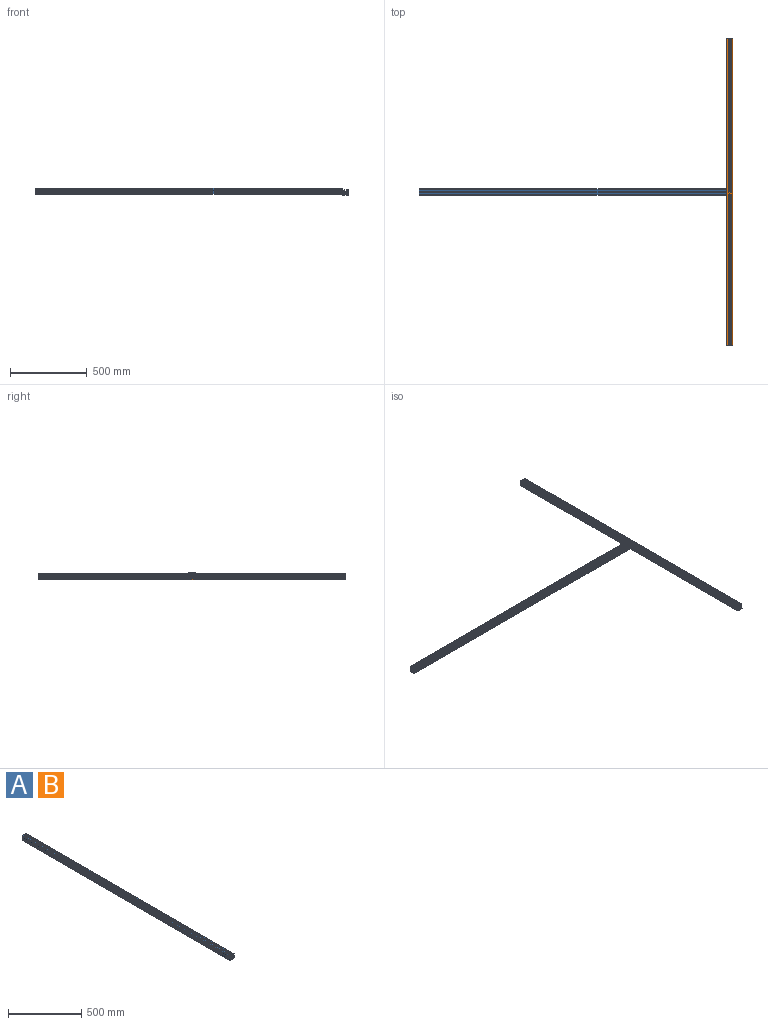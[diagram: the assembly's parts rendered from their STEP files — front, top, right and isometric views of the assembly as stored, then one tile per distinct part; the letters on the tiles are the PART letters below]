
ASSEMBLY  parts=2 mates=1
PART A: 155 faces, bbox 40x2000x40 mm
  f0: cylinder r=3.4mm len=2000mm, axis (0,-1,0), area 42725.7mm2, adj f1,f2
  f1: plane 40x40mm, normal (0,-1,0), area 657mm2, adj f0,f3,f4,f5,f6,f7,f8,f9
  f2: plane 40x40mm, normal (0,1,0), area 657mm2, adj f0,f3,f4,f5,f6,f7,f8,f9
  f3: cylinder r=1.5mm len=2000mm, axis (0,-1,0), area 4712.4mm2, adj f1,f2,f4,f122
  f4: plane 2000x10.5mm, normal (-1,0,0), area 21000mm2, adj f1,f2,f3,f5
  f5: cylinder r=4mm len=2000mm, axis (0,-1,0), area 12566.4mm2, adj f1,f2,f4,f6
  f6: plane 2000x10.5mm, normal (0,0,-1), area 21000mm2, adj f1,f2,f5,f7
  f7: cylinder r=1.5mm len=2000mm, axis (0,-1,0), area 4712.4mm2, adj f1,f2,f6,f8
  f8: plane 2000x2mm, normal (1,0,0), area 4000mm2, adj f1,f2,f7,f9
  f9: cylinder r=1mm len=2000mm, axis (0,-1,0), area 3141.6mm2, adj f1,f2,f8,f10
  f10: plane 2000x1.5mm, normal (0,0,1), area 3000mm2, adj f1,f2,f9,f11
  f11: cylinder r=0.5mm len=2000mm, axis (0,-1,0), area 1570.8mm2, adj f1,f2,f10,f12
  f12: plane 2000x1.55mm, normal (-1,0,0), area 3100mm2, adj f1,f2,f11,f13
  f13: cylinder r=0.45mm len=2000mm, axis (0,-1,0), area 1413.7mm2, adj f1,f2,f12,f14
  f14: plane 2000x0.05mm, normal (0,0,1), area 100mm2, adj f1,f2,f13,f15
  f15: cylinder r=2.5mm len=2000mm, axis (0,-1,0), area 7854mm2, adj f1,f2,f14,f16
  f16: plane 2000x1.31mm, normal (1,0,0), area 2615.2mm2, adj f1,f2,f15,f17
  f17: cylinder r=5mm len=2000mm, axis (0,-1,0), area 7854mm2, adj f1,f2,f16,f18
  f18: plane 2000x1.44mm, normal (0.71,0,-0.71), area 4079.7mm2, adj f1,f2,f17,f19
  f19: cylinder r=5mm len=2000mm, axis (0,-1,0), area 7854mm2, adj f1,f2,f18,f20
  f20: plane 2000x7.12mm, normal (0,0,-1), area 14230.4mm2, adj f1,f2,f19,f21
  f21: cylinder r=5mm len=2000mm, axis (0,-1,0), area 7854mm2, adj f1,f2,f20,f22
  f22: plane 2000x1.44mm, normal (-0.71,0,-0.71), area 4079.7mm2, adj f1,f2,f21,f23
  f23: cylinder r=5mm len=2000mm, axis (0,-1,0), area 7854mm2, adj f1,f2,f22,f24
  f24: plane 2000x1.31mm, normal (-1,0,0), area 2615.2mm2, adj f1,f2,f23,f25
  f25: cylinder r=2.5mm len=2000mm, axis (0,-1,0), area 7854mm2, adj f1,f2,f24,f26
  f26: plane 2000x0.05mm, normal (0,0,1), area 100mm2, adj f1,f2,f25,f27
  f27: cylinder r=0.45mm len=2000mm, axis (0,-1,0), area 1413.7mm2, adj f1,f2,f26,f28
  f28: plane 2000x1.55mm, normal (1,0,0), area 3100mm2, adj f1,f2,f27,f29
  f29: cylinder r=0.5mm len=2000mm, axis (0,-1,0), area 1570.8mm2, adj f1,f2,f28,f30
  f30: plane 2000x1.5mm, normal (0,0,1), area 3000mm2, adj f1,f2,f29,f31
  f31: cylinder r=1mm len=2000mm, axis (0,-1,0), area 3141.6mm2, adj f1,f2,f30,f32
  f32: plane 2000x2mm, normal (-1,0,0), area 4000mm2, adj f1,f2,f31,f33
  f33: cylinder r=1.5mm len=2000mm, axis (0,-1,0), area 4712.4mm2, adj f1,f2,f32,f34
  f34: plane 2000x10.5mm, normal (0,0,-1), area 21000mm2, adj f1,f2,f33,f35
  f35: cylinder r=4mm len=2000mm, axis (0,-1,0), area 12566.4mm2, adj f1,f2,f34,f36
  f36: plane 2000x10.5mm, normal (1,0,0), area 21000mm2, adj f1,f2,f35,f37
  f37: cylinder r=1.5mm len=2000mm, axis (0,-1,0), area 4712.4mm2, adj f1,f2,f36,f38
  f38: plane 2000x2mm, normal (0,0,1), area 4000mm2, adj f1,f2,f37,f39
  f39: cylinder r=1mm len=2000mm, axis (0,-1,0), area 3141.6mm2, adj f1,f2,f38,f40
  f40: plane 2000x1.5mm, normal (-1,0,0), area 3000mm2, adj f1,f2,f39,f41
  f41: cylinder r=0.5mm len=2000mm, axis (0,-1,0), area 1570.8mm2, adj f1,f2,f40,f42
  f42: plane 2000x1.55mm, normal (0,0,-1), area 3100mm2, adj f1,f2,f41,f43
  f43: cylinder r=0.45mm len=2000mm, axis (0,-1,0), area 1413.7mm2, adj f1,f2,f42,f44
  f44: plane 2000x0.05mm, normal (-1,0,0), area 100mm2, adj f1,f2,f43,f45
  f45: cylinder r=2.5mm len=2000mm, axis (0,-1,0), area 7854mm2, adj f1,f2,f44,f46
  f46: plane 2000x1.31mm, normal (0,0,1), area 2615.2mm2, adj f1,f2,f45,f47
  f47: cylinder r=5mm len=2000mm, axis (0,-1,0), area 7854mm2, adj f1,f2,f46,f48
  f48: plane 2000x1.44mm, normal (0.71,0,0.71), area 4079.7mm2, adj f1,f2,f47,f49
  f49: cylinder r=5mm len=2000mm, axis (0,-1,0), area 7854mm2, adj f1,f2,f48,f50
  f50: plane 2000x7.12mm, normal (1,0,0), area 14230.4mm2, adj f1,f2,f49,f51
  f51: cylinder r=5mm len=2000mm, axis (0,-1,0), area 7854mm2, adj f1,f2,f50,f52
  f52: plane 2000x1.44mm, normal (0.71,0,-0.71), area 4079.7mm2, adj f1,f2,f51,f53
  f53: cylinder r=5mm len=2000mm, axis (0,-1,0), area 7854mm2, adj f1,f2,f52,f54
  f54: plane 2000x1.31mm, normal (0,0,-1), area 2615.2mm2, adj f1,f2,f53,f55
  f55: cylinder r=2.5mm len=2000mm, axis (0,-1,0), area 7854mm2, adj f1,f2,f54,f56
  f56: plane 2000x0.05mm, normal (-1,0,0), area 100mm2, adj f1,f2,f55,f57
  f57: cylinder r=0.45mm len=2000mm, axis (0,-1,0), area 1413.7mm2, adj f1,f2,f56,f58
  f58: plane 2000x1.55mm, normal (0,0,1), area 3100mm2, adj f1,f2,f57,f59
  f59: cylinder r=0.5mm len=2000mm, axis (0,-1,0), area 1570.8mm2, adj f1,f2,f58,f60
  f60: plane 2000x1.5mm, normal (-1,0,0), area 3000mm2, adj f1,f2,f59,f61
  f61: cylinder r=1mm len=2000mm, axis (0,-1,0), area 3141.6mm2, adj f1,f2,f60,f62
  f62: plane 2000x2mm, normal (0,0,-1), area 4000mm2, adj f1,f2,f61,f63
  f63: cylinder r=1.5mm len=2000mm, axis (0,-1,0), area 4712.4mm2, adj f1,f2,f62,f64
  f64: plane 2000x10.5mm, normal (1,0,0), area 21000mm2, adj f1,f2,f63,f65
  f65: cylinder r=4mm len=2000mm, axis (0,-1,0), area 12566.4mm2, adj f1,f2,f64,f66
  f66: plane 2000x10.5mm, normal (0,0,1), area 21000mm2, adj f1,f2,f65,f67
  f67: cylinder r=1.5mm len=2000mm, axis (0,-1,0), area 4712.4mm2, adj f1,f2,f66,f68
  f68: plane 2000x2mm, normal (-1,0,0), area 4000mm2, adj f1,f2,f67,f69
  f69: cylinder r=1mm len=2000mm, axis (0,-1,0), area 3141.6mm2, adj f1,f2,f68,f70
  f70: plane 2000x1.5mm, normal (0,0,-1), area 3000mm2, adj f1,f2,f69,f71
  f71: cylinder r=0.5mm len=2000mm, axis (0,-1,0), area 1570.8mm2, adj f1,f2,f70,f72
  f72: plane 2000x1.55mm, normal (1,0,0), area 3100mm2, adj f1,f2,f71,f73
  f73: cylinder r=0.45mm len=2000mm, axis (0,-1,0), area 1413.7mm2, adj f1,f2,f72,f74
  f74: plane 2000x0.05mm, normal (0,0,-1), area 100mm2, adj f1,f2,f73,f75
  f75: cylinder r=2.5mm len=2000mm, axis (0,-1,0), area 7854mm2, adj f1,f2,f74,f76
  f76: plane 2000x1.31mm, normal (-1,0,0), area 2615.2mm2, adj f1,f2,f75,f77
  f77: cylinder r=5mm len=2000mm, axis (0,-1,0), area 7854mm2, adj f1,f2,f76,f78
  f78: plane 2000x1.44mm, normal (-0.71,0,0.71), area 4079.7mm2, adj f1,f2,f77,f79
  f79: cylinder r=5mm len=2000mm, axis (0,-1,0), area 7854mm2, adj f1,f2,f78,f80
  f80: plane 2000x7.12mm, normal (0,0,1), area 14230.4mm2, adj f1,f2,f79,f81
  f81: cylinder r=5mm len=2000mm, axis (0,-1,0), area 7854mm2, adj f1,f2,f80,f82
  f82: plane 2000x1.44mm, normal (0.71,0,0.71), area 4079.7mm2, adj f1,f2,f81,f83
  f83: cylinder r=5mm len=2000mm, axis (0,-1,0), area 7854mm2, adj f1,f2,f82,f84
  f84: plane 2000x1.31mm, normal (1,0,0), area 2615.2mm2, adj f1,f2,f83,f85
  f85: cylinder r=2.5mm len=2000mm, axis (0,-1,0), area 7854mm2, adj f1,f2,f84,f86
  f86: plane 2000x0.05mm, normal (0,0,-1), area 100mm2, adj f1,f2,f85,f87
  f87: cylinder r=0.45mm len=2000mm, axis (0,-1,0), area 1413.7mm2, adj f1,f2,f86,f88
  f88: plane 2000x1.55mm, normal (-1,0,0), area 3100mm2, adj f1,f2,f87,f89
  f89: cylinder r=0.5mm len=2000mm, axis (0,-1,0), area 1570.8mm2, adj f1,f2,f88,f90
  f90: plane 2000x1.5mm, normal (0,0,-1), area 3000mm2, adj f1,f2,f89,f91
  f91: cylinder r=1mm len=2000mm, axis (0,-1,0), area 3141.6mm2, adj f1,f2,f90,f92
  f92: plane 2000x2mm, normal (1,0,0), area 4000mm2, adj f1,f2,f91,f93
  f93: cylinder r=1.5mm len=2000mm, axis (0,-1,0), area 4712.4mm2, adj f1,f2,f92,f94
  f94: plane 2000x10.5mm, normal (0,0,1), area 21000mm2, adj f1,f2,f93,f95
  f95: cylinder r=4mm len=2000mm, axis (0,-1,0), area 12566.4mm2, adj f1,f2,f94,f96
  f96: plane 2000x10.5mm, normal (-1,0,0), area 21000mm2, adj f1,f2,f95,f97
  f97: cylinder r=1.5mm len=2000mm, axis (0,-1,0), area 4712.4mm2, adj f1,f2,f96,f98
  f98: plane 2000x2mm, normal (0,0,-1), area 4000mm2, adj f1,f2,f97,f99
  f99: cylinder r=1mm len=2000mm, axis (0,-1,0), area 3141.6mm2, adj f1,f2,f98,f100
  f100: plane 2000x1.5mm, normal (1,0,0), area 3000mm2, adj f1,f2,f99,f101
  f101: cylinder r=0.5mm len=2000mm, axis (0,-1,0), area 1570.8mm2, adj f1,f2,f100,f102
  f102: plane 2000x1.55mm, normal (0,0,1), area 3100mm2, adj f1,f2,f101,f103
  f103: cylinder r=0.45mm len=2000mm, axis (0,-1,0), area 1413.7mm2, adj f1,f2,f102,f104
  f104: plane 2000x0.05mm, normal (1,0,0), area 100mm2, adj f1,f2,f103,f105
  f105: cylinder r=2.5mm len=2000mm, axis (0,-1,0), area 7854mm2, adj f1,f2,f104,f106
  f106: plane 2000x1.31mm, normal (0,0,-1), area 2615.2mm2, adj f1,f2,f105,f107
  f107: cylinder r=5mm len=2000mm, axis (0,-1,0), area 7854mm2, adj f1,f2,f106,f108
  f108: plane 2000x1.44mm, normal (-0.71,0,-0.71), area 4079.7mm2, adj f1,f2,f107,f109
  f109: cylinder r=5mm len=2000mm, axis (0,-1,0), area 7854mm2, adj f1,f2,f108,f110
  f110: plane 2000x7.12mm, normal (-1,0,0), area 14230.4mm2, adj f1,f2,f109,f111
  f111: cylinder r=5mm len=2000mm, axis (0,-1,0), area 7854mm2, adj f1,f2,f110,f112
  f112: plane 2000x1.44mm, normal (-0.71,0,0.71), area 4079.7mm2, adj f1,f2,f111,f113
  f113: cylinder r=5mm len=2000mm, axis (0,-1,0), area 7854mm2, adj f1,f2,f112,f114
  f114: plane 2000x1.31mm, normal (0,0,1), area 2615.2mm2, adj f1,f2,f113,f115
  f115: cylinder r=2.5mm len=2000mm, axis (0,-1,0), area 7854mm2, adj f1,f2,f114,f116
  f116: plane 2000x0.05mm, normal (1,0,0), area 100mm2, adj f1,f2,f115,f117
  f117: cylinder r=0.45mm len=2000mm, axis (0,-1,0), area 1413.7mm2, adj f1,f2,f116,f118
  f118: plane 2000x1.55mm, normal (0,0,-1), area 3100mm2, adj f1,f2,f117,f119
  f119: cylinder r=0.5mm len=2000mm, axis (0,-1,0), area 1570.8mm2, adj f1,f2,f118,f120
  f120: plane 2000x1.5mm, normal (1,0,0), area 3000mm2, adj f1,f2,f119,f121
  f121: cylinder r=1mm len=2000mm, axis (0,-1,0), area 3141.6mm2, adj f1,f2,f120,f122
  f122: plane 2000x2mm, normal (0,0,1), area 4000mm2, adj f1,f2,f3,f121
  f123: cylinder r=0.5mm len=2000mm, axis (0,-1,0), area 1570.8mm2, adj f1,f2,f124,f130
  f124: plane 2000x5.4mm, normal (0,0,1), area 10800mm2, adj f1,f2,f123,f125
  f125: cylinder r=0.5mm len=2000mm, axis (0,-1,0), area 1570.8mm2, adj f1,f2,f124,f126
  f126: plane 2000x5.4mm, normal (1,0,0), area 10800mm2, adj f1,f2,f125,f127
  f127: cylinder r=0.5mm len=2000mm, axis (0,-1,0), area 1570.8mm2, adj f1,f2,f126,f128
  f128: plane 2000x3.7mm, normal (0,0,-1), area 7400mm2, adj f1,f2,f127,f129
  f129: cylinder r=2.2mm len=2000mm, axis (0,-1,0), area 6911.5mm2, adj f1,f2,f128,f130
  f130: plane 2000x3.7mm, normal (-1,0,0), area 7400mm2, adj f1,f2,f123,f129
  f131: cylinder r=0.5mm len=2000mm, axis (0,-1,0), area 1570.8mm2, adj f1,f2,f132,f138
  f132: plane 2000x5.4mm, normal (1,0,0), area 10800mm2, adj f1,f2,f131,f133
  f133: cylinder r=0.5mm len=2000mm, axis (0,-1,0), area 1570.8mm2, adj f1,f2,f132,f134
  f134: plane 2000x5.4mm, normal (0,0,-1), area 10800mm2, adj f1,f2,f133,f135
  f135: cylinder r=0.5mm len=2000mm, axis (0,-1,0), area 1570.8mm2, adj f1,f2,f134,f136
  f136: plane 2000x3.7mm, normal (-1,0,0), area 7400mm2, adj f1,f2,f135,f137
  f137: cylinder r=2.2mm len=2000mm, axis (0,-1,0), area 6911.5mm2, adj f1,f2,f136,f138
  f138: plane 2000x3.7mm, normal (0,0,1), area 7400mm2, adj f1,f2,f131,f137
  f139: cylinder r=0.5mm len=2000mm, axis (0,-1,0), area 1570.8mm2, adj f1,f2,f140,f146
  f140: plane 2000x5.4mm, normal (0,0,-1), area 10800mm2, adj f1,f2,f139,f141
  f141: cylinder r=0.5mm len=2000mm, axis (0,-1,0), area 1570.8mm2, adj f1,f2,f140,f142
  f142: plane 2000x5.4mm, normal (-1,0,0), area 10800mm2, adj f1,f2,f141,f143
  f143: cylinder r=0.5mm len=2000mm, axis (0,-1,0), area 1570.8mm2, adj f1,f2,f142,f144
  f144: plane 2000x3.7mm, normal (0,0,1), area 7400mm2, adj f1,f2,f143,f145
  f145: cylinder r=2.2mm len=2000mm, axis (0,-1,0), area 6911.5mm2, adj f1,f2,f144,f146
  f146: plane 2000x3.7mm, normal (1,0,0), area 7400mm2, adj f1,f2,f139,f145
  f147: cylinder r=0.5mm len=2000mm, axis (0,-1,0), area 1570.8mm2, adj f1,f2,f148,f154
  f148: plane 2000x5.4mm, normal (-1,0,0), area 10800mm2, adj f1,f2,f147,f149
  f149: cylinder r=0.5mm len=2000mm, axis (0,-1,0), area 1570.8mm2, adj f1,f2,f148,f150
  f150: plane 2000x5.4mm, normal (0,0,1), area 10800mm2, adj f1,f2,f149,f151
  f151: cylinder r=0.5mm len=2000mm, axis (0,-1,0), area 1570.8mm2, adj f1,f2,f150,f152
  f152: plane 2000x3.7mm, normal (1,0,0), area 7400mm2, adj f1,f2,f151,f153
  f153: cylinder r=2.2mm len=2000mm, axis (0,-1,0), area 6911.5mm2, adj f1,f2,f152,f154
  f154: plane 2000x3.7mm, normal (0,0,-1), area 7400mm2, adj f1,f2,f147,f153
PART B: same geometry as A
PLACE A rot(axis=(-0.58,0.58,0.58),120deg) t=(-1230.26,-13.79,120.1)mm
PLACE B rot(axis=(0.45,-0.8,-0.41),0deg) t=(-210.26,-13.79,109.35)mm
MATE fastened A.f0 <-> B.f96  axis (1,0,0) through (-230.26,-13.79,120.1)mm
